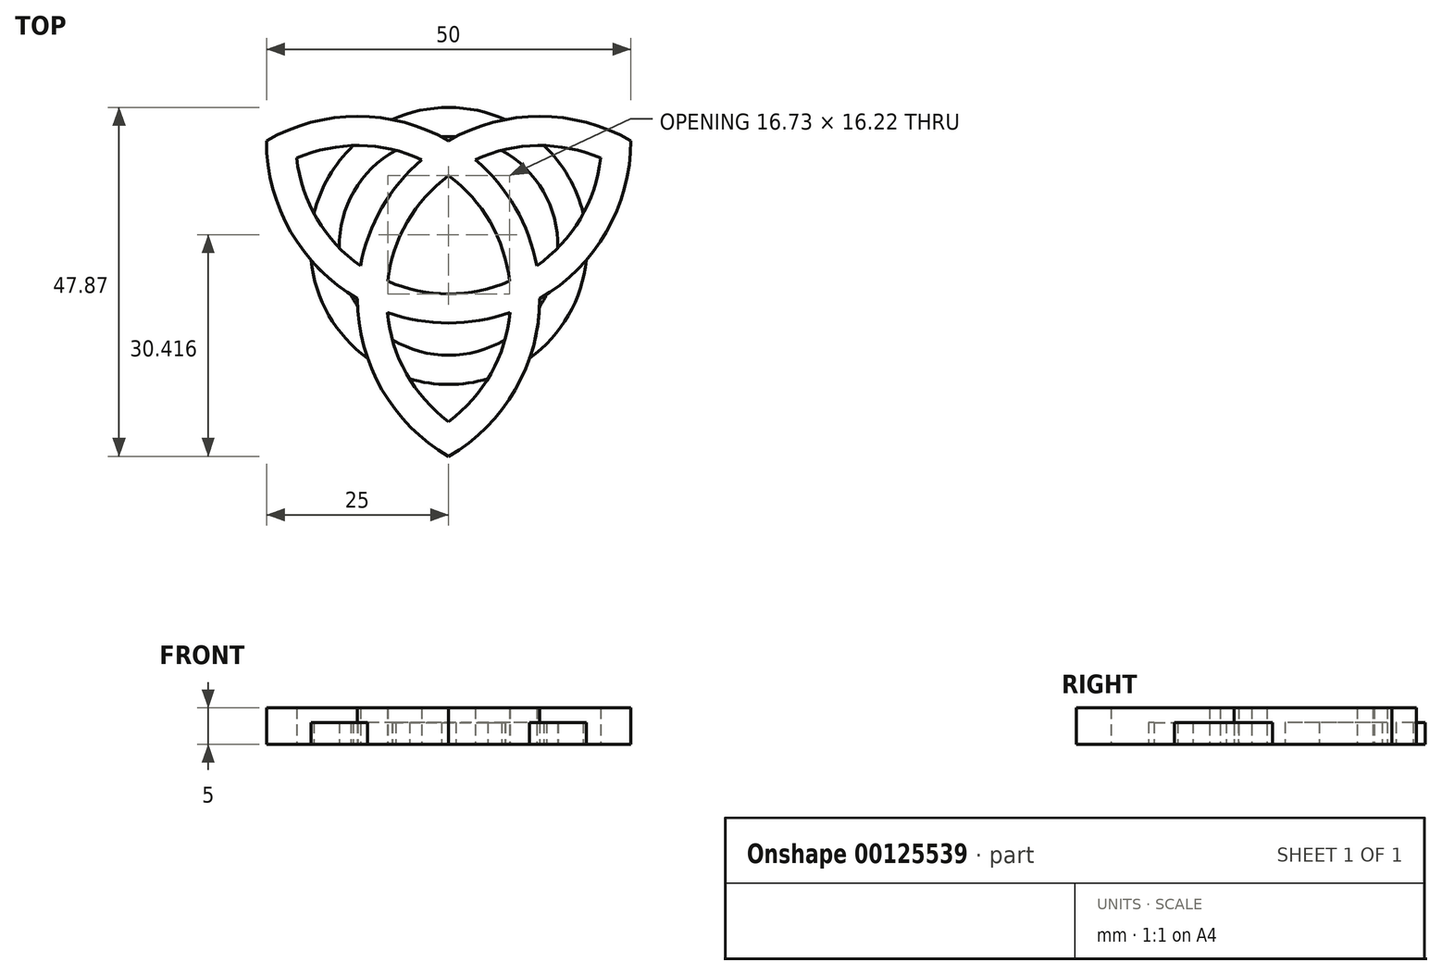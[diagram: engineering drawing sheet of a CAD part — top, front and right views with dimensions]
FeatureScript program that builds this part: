
annotation { "Feature Type Name" : "Feature", "Feature Type Description" : "" }
export const myFeature = defineFeature(function(context is Context, id is Id, definition is map)
    precondition{}
    {
        {
            var Q0;
            Q0=qCreatedBy(makeId("Top.planeOp"),FACE);
            var sketch = newSketch(context, id + "F0", { "sketchPlane" : qUnion([Q0])});
            skCircle(sketch, "E0.cCircle", {"center": v(0, 0) * mm, "radius": 14.43 * mm, "construction": true});
            skLineSegment(sketch, "E0.0", {"start": v(-25, 14.43) * mm, "end": v(25, 14.43) * mm, "construction": true});
            skLineSegment(sketch, "E0.1", {"start": v(25, 14.43) * mm, "end": v(0, -28.87) * mm, "construction": true});
            skLineSegment(sketch, "E0.2", {"start": v(0, -28.87) * mm, "end": v(-25, 14.43) * mm, "construction": true});
            skPoint(sketch, "E0.0.midPoint", {"position": v(0, 14.43) * mm});
            skCircle(sketch, "E1", {"center": v(0, 14.43) * mm, "radius": 25 * mm});
            skCircle(sketch, "E2", {"center": v(12.5, -7.22) * mm, "radius": 25 * mm});
            skCircle(sketch, "E3", {"center": v(-12.5, -7.22) * mm, "radius": 25 * mm});
            skCircle(sketch, "E4.0", {"center": v(-12.5, -7.22) * mm, "radius": 21 * mm});
            skCircle(sketch, "E5.0", {"center": v(0, 14.43) * mm, "radius": 21 * mm});
            skCircle(sketch, "E6.0", {"center": v(12.5, -7.22) * mm, "radius": 21 * mm});
            skCircle(sketch, "E7", {"center": v(0, 0) * mm, "radius": 19 * mm});
            skCircle(sketch, "E8.0", {"center": v(0, 0) * mm, "radius": 15 * mm});
            skSolve(sketch);
        }
        {
            var Q0;
            {var subQ0=sQuery(id+"F0.wireOp",EDGE,"E2");var subQ1=sQuery(id+"F0.wireOp",EDGE,"E1");var subQ2=makeQuery(id+"F0.imprint","INTERSECT",VERTEX,{"disambiguationData":[OD(0.0)],"derivedFrom":[subQ1,subQ0]});Q0=makeQuery(id+"F0.imprint","IMPRINT",FACE,{"disambiguationData":[TD([[makeQuery(id+"F0.imprint","IMPRINT",EDGE,{"disambiguationData":[TD([[subQ2,1.0]])],"derivedFrom":subQ1}),1.0]])]});}
            var Q1;
            {var subQ0=sQuery(id+"F0.wireOp",EDGE,"E7");var subQ1=sQuery(id+"F0.wireOp",EDGE,"E1");var subQ2=makeQuery(id+"F0.imprint","INTERSECT",VERTEX,{"disambiguationData":[OD(1.0)],"derivedFrom":[subQ1,subQ0]});Q1=makeQuery(id+"F0.imprint","IMPRINT",FACE,{"disambiguationData":[TD([[makeQuery(id+"F0.imprint","IMPRINT",EDGE,{"disambiguationData":[TD([[subQ2,-1.0]])],"derivedFrom":subQ1}),1.0]])]});}
            var Q2;
            {var subQ0=sQuery(id+"F0.wireOp",EDGE,"E8.0");var subQ1=sQuery(id+"F0.wireOp",EDGE,"E1");var subQ2=makeQuery(id+"F0.imprint","INTERSECT",VERTEX,{"disambiguationData":[OD(1.0)],"derivedFrom":[subQ1,subQ0]});Q2=makeQuery(id+"F0.imprint","IMPRINT",FACE,{"disambiguationData":[TD([[makeQuery(id+"F0.imprint","IMPRINT",EDGE,{"disambiguationData":[TD([[subQ2,-1.0]])],"derivedFrom":subQ1}),1.0]])]});}
            var Q3;
            {var subQ0=sQuery(id+"F0.wireOp",EDGE,"E3");var subQ1=sQuery(id+"F0.wireOp",EDGE,"E1");var subQ2=makeQuery(id+"F0.imprint","INTERSECT",VERTEX,{"disambiguationData":[OD(1.0)],"derivedFrom":[subQ1,subQ0]});Q3=makeQuery(id+"F0.imprint","IMPRINT",FACE,{"disambiguationData":[TD([[makeQuery(id+"F0.imprint","IMPRINT",EDGE,{"disambiguationData":[TD([[subQ2,-1.0]])],"derivedFrom":subQ1}),1.0]])]});}
            var Q4;
            {var subQ0=sQuery(id+"F0.wireOp",EDGE,"E4.0");var subQ1=sQuery(id+"F0.wireOp",EDGE,"E1");var subQ2=makeQuery(id+"F0.imprint","INTERSECT",VERTEX,{"disambiguationData":[OD(1.0)],"derivedFrom":[subQ1,subQ0]});Q4=makeQuery(id+"F0.imprint","IMPRINT",FACE,{"disambiguationData":[TD([[makeQuery(id+"F0.imprint","IMPRINT",EDGE,{"disambiguationData":[TD([[subQ2,-1.0]])],"derivedFrom":subQ1}),1.0]])]});}
            var Q5;
            {var subQ0=sQuery(id+"F0.wireOp",EDGE,"E6.0");var subQ1=sQuery(id+"F0.wireOp",EDGE,"E1");var subQ2=makeQuery(id+"F0.imprint","INTERSECT",VERTEX,{"disambiguationData":[OD(0.0)],"derivedFrom":[subQ1,subQ0]});Q5=makeQuery(id+"F0.imprint","IMPRINT",FACE,{"disambiguationData":[TD([[makeQuery(id+"F0.imprint","IMPRINT",EDGE,{"disambiguationData":[TD([[subQ2,-1.0]])],"derivedFrom":subQ1}),1.0]])]});}
            var Q6;
            {var subQ0=sQuery(id+"F0.wireOp",EDGE,"E2");var subQ1=sQuery(id+"F0.wireOp",EDGE,"E1");var subQ2=makeQuery(id+"F0.imprint","INTERSECT",VERTEX,{"disambiguationData":[OD(1.0)],"derivedFrom":[subQ1,subQ0]});Q6=makeQuery(id+"F0.imprint","IMPRINT",FACE,{"disambiguationData":[TD([[makeQuery(id+"F0.imprint","IMPRINT",EDGE,{"disambiguationData":[TD([[subQ2,-1.0]])],"derivedFrom":subQ1}),1.0]])]});}
            var Q7;
            {var subQ0=sQuery(id+"F0.wireOp",EDGE,"E8.0");var subQ1=sQuery(id+"F0.wireOp",EDGE,"E1");var subQ2=makeQuery(id+"F0.imprint","INTERSECT",VERTEX,{"disambiguationData":[OD(0.0)],"derivedFrom":[subQ1,subQ0]});Q7=makeQuery(id+"F0.imprint","IMPRINT",FACE,{"disambiguationData":[TD([[makeQuery(id+"F0.imprint","IMPRINT",EDGE,{"disambiguationData":[TD([[subQ2,-1.0]])],"derivedFrom":subQ1}),1.0]])]});}
            var Q8;
            {var subQ0=sQuery(id+"F0.wireOp",EDGE,"E7");var subQ1=sQuery(id+"F0.wireOp",EDGE,"E1");var subQ2=makeQuery(id+"F0.imprint","INTERSECT",VERTEX,{"disambiguationData":[OD(0.0)],"derivedFrom":[subQ1,subQ0]});Q8=makeQuery(id+"F0.imprint","IMPRINT",FACE,{"disambiguationData":[TD([[makeQuery(id+"F0.imprint","IMPRINT",EDGE,{"disambiguationData":[TD([[subQ2,-1.0]])],"derivedFrom":subQ1}),1.0]])]});}
            var Q9;
            {var subQ0=sQuery(id+"F0.wireOp",EDGE,"E4.0");var subQ1=sQuery(id+"F0.wireOp",EDGE,"E1");var subQ2=makeQuery(id+"F0.imprint","INTERSECT",VERTEX,{"disambiguationData":[OD(0.0)],"derivedFrom":[subQ1,subQ0]});Q9=makeQuery(id+"F0.imprint","IMPRINT",FACE,{"disambiguationData":[TD([[makeQuery(id+"F0.imprint","IMPRINT",EDGE,{"disambiguationData":[TD([[subQ2,-1.0]])],"derivedFrom":subQ1}),1.0]])]});}
            var Q10;
            {var subQ0=sQuery(id+"F0.wireOp",EDGE,"E3");var subQ1=sQuery(id+"F0.wireOp",EDGE,"E1");var subQ2=makeQuery(id+"F0.imprint","INTERSECT",VERTEX,{"disambiguationData":[OD(0.0)],"derivedFrom":[subQ1,subQ0]});Q10=makeQuery(id+"F0.imprint","IMPRINT",FACE,{"disambiguationData":[TD([[makeQuery(id+"F0.imprint","IMPRINT",EDGE,{"disambiguationData":[TD([[subQ2,-1.0]])],"derivedFrom":subQ1}),1.0]])]});}
            var Q11;
            {var subQ0=sQuery(id+"F0.wireOp",EDGE,"E7");var subQ1=sQuery(id+"F0.wireOp",EDGE,"E3");var subQ2=makeQuery(id+"F0.imprint","INTERSECT",VERTEX,{"disambiguationData":[OD(0.0)],"derivedFrom":[subQ1,subQ0]});Q11=makeQuery(id+"F0.imprint","IMPRINT",FACE,{"disambiguationData":[TD([[makeQuery(id+"F0.imprint","IMPRINT",EDGE,{"disambiguationData":[TD([[subQ2,-1.0]])],"derivedFrom":subQ1}),1.0]])]});}
            var Q12;
            {var subQ0=sQuery(id+"F0.wireOp",EDGE,"E8.0");var subQ1=sQuery(id+"F0.wireOp",EDGE,"E3");var subQ2=makeQuery(id+"F0.imprint","INTERSECT",VERTEX,{"disambiguationData":[OD(0.0)],"derivedFrom":[subQ1,subQ0]});Q12=makeQuery(id+"F0.imprint","IMPRINT",FACE,{"disambiguationData":[TD([[makeQuery(id+"F0.imprint","IMPRINT",EDGE,{"disambiguationData":[TD([[subQ2,-1.0]])],"derivedFrom":subQ1}),1.0]])]});}
            var Q13;
            {var subQ0=sQuery(id+"F0.wireOp",EDGE,"E3");var subQ1=sQuery(id+"F0.wireOp",EDGE,"E2");var subQ2=makeQuery(id+"F0.imprint","INTERSECT",VERTEX,{"disambiguationData":[OD(1.0)],"derivedFrom":[subQ1,subQ0]});Q13=makeQuery(id+"F0.imprint","IMPRINT",FACE,{"disambiguationData":[TD([[makeQuery(id+"F0.imprint","IMPRINT",EDGE,{"disambiguationData":[TD([[subQ2,-1.0]])],"derivedFrom":subQ1}),-1.0]])]});}
            var Q14;
            {var subQ0=sQuery(id+"F0.wireOp",EDGE,"E3");var subQ1=sQuery(id+"F0.wireOp",EDGE,"E2");var subQ2=makeQuery(id+"F0.imprint","INTERSECT",VERTEX,{"disambiguationData":[OD(1.0)],"derivedFrom":[subQ1,subQ0]});Q14=makeQuery(id+"F0.imprint","IMPRINT",FACE,{"disambiguationData":[TD([[makeQuery(id+"F0.imprint","IMPRINT",EDGE,{"disambiguationData":[TD([[subQ2,-1.0]])],"derivedFrom":subQ1}),1.0]])]});}
            var Q15;
            {var subQ0=sQuery(id+"F0.wireOp",EDGE,"E5.0");var subQ1=sQuery(id+"F0.wireOp",EDGE,"E3");var subQ2=makeQuery(id+"F0.imprint","INTERSECT",VERTEX,{"disambiguationData":[OD(0.0)],"derivedFrom":[subQ1,subQ0]});Q15=makeQuery(id+"F0.imprint","IMPRINT",FACE,{"disambiguationData":[TD([[makeQuery(id+"F0.imprint","IMPRINT",EDGE,{"disambiguationData":[TD([[subQ2,-1.0]])],"derivedFrom":subQ1}),1.0]])]});}
            var Q16;
            {var subQ0=sQuery(id+"F0.wireOp",EDGE,"E4.0");var subQ1=sQuery(id+"F0.wireOp",EDGE,"E1");var subQ2=makeQuery(id+"F0.imprint","INTERSECT",VERTEX,{"disambiguationData":[OD(1.0)],"derivedFrom":[subQ1,subQ0]});Q16=makeQuery(id+"F0.imprint","IMPRINT",FACE,{"disambiguationData":[TD([[makeQuery(id+"F0.imprint","IMPRINT",EDGE,{"disambiguationData":[TD([[subQ2,-1.0]])],"derivedFrom":subQ1}),-1.0]])]});}
            var Q17;
            {var subQ0=sQuery(id+"F0.wireOp",EDGE,"E7");var subQ1=sQuery(id+"F0.wireOp",EDGE,"E3");var subQ2=makeQuery(id+"F0.imprint","INTERSECT",VERTEX,{"disambiguationData":[OD(1.0)],"derivedFrom":[subQ1,subQ0]});Q17=makeQuery(id+"F0.imprint","IMPRINT",FACE,{"disambiguationData":[TD([[makeQuery(id+"F0.imprint","IMPRINT",EDGE,{"disambiguationData":[TD([[subQ2,-1.0]])],"derivedFrom":subQ1}),1.0]])]});}
            var Q18;
            {var subQ0=sQuery(id+"F0.wireOp",EDGE,"E6.0");var subQ1=sQuery(id+"F0.wireOp",EDGE,"E3");var subQ2=makeQuery(id+"F0.imprint","INTERSECT",VERTEX,{"disambiguationData":[OD(1.0)],"derivedFrom":[subQ1,subQ0]});Q18=makeQuery(id+"F0.imprint","IMPRINT",FACE,{"disambiguationData":[TD([[makeQuery(id+"F0.imprint","IMPRINT",EDGE,{"disambiguationData":[TD([[subQ2,-1.0]])],"derivedFrom":subQ1}),1.0]])]});}
            var Q19;
            {var subQ0=sQuery(id+"F0.wireOp",EDGE,"E3");var subQ1=sQuery(id+"F0.wireOp",EDGE,"E2");var subQ2=makeQuery(id+"F0.imprint","INTERSECT",VERTEX,{"disambiguationData":[OD(0.0)],"derivedFrom":[subQ1,subQ0]});Q19=makeQuery(id+"F0.imprint","IMPRINT",FACE,{"disambiguationData":[TD([[makeQuery(id+"F0.imprint","IMPRINT",EDGE,{"disambiguationData":[TD([[subQ2,1.0]])],"derivedFrom":subQ1}),1.0]])]});}
            var Q20;
            {var subQ0=sQuery(id+"F0.wireOp",EDGE,"E7");var subQ1=sQuery(id+"F0.wireOp",EDGE,"E2");var subQ2=makeQuery(id+"F0.imprint","INTERSECT",VERTEX,{"disambiguationData":[OD(1.0)],"derivedFrom":[subQ1,subQ0]});Q20=makeQuery(id+"F0.imprint","IMPRINT",FACE,{"disambiguationData":[TD([[makeQuery(id+"F0.imprint","IMPRINT",EDGE,{"disambiguationData":[TD([[subQ2,-1.0]])],"derivedFrom":subQ1}),1.0]])]});}
            var Q21;
            {var subQ0=sQuery(id+"F0.wireOp",EDGE,"E8.0");var subQ1=sQuery(id+"F0.wireOp",EDGE,"E2");var subQ2=makeQuery(id+"F0.imprint","INTERSECT",VERTEX,{"disambiguationData":[OD(1.0)],"derivedFrom":[subQ1,subQ0]});Q21=makeQuery(id+"F0.imprint","IMPRINT",FACE,{"disambiguationData":[TD([[makeQuery(id+"F0.imprint","IMPRINT",EDGE,{"disambiguationData":[TD([[subQ2,-1.0]])],"derivedFrom":subQ1}),1.0]])]});}
            var Q22;
            {var subQ0=sQuery(id+"F0.wireOp",EDGE,"E2");var subQ1=sQuery(id+"F0.wireOp",EDGE,"E1");var subQ2=makeQuery(id+"F0.imprint","INTERSECT",VERTEX,{"disambiguationData":[OD(1.0)],"derivedFrom":[subQ1,subQ0]});Q22=makeQuery(id+"F0.imprint","IMPRINT",FACE,{"disambiguationData":[TD([[makeQuery(id+"F0.imprint","IMPRINT",EDGE,{"disambiguationData":[TD([[subQ2,-1.0]])],"derivedFrom":subQ1}),-1.0]])]});}
            var Q23;
            {var subQ0=sQuery(id+"F0.wireOp",EDGE,"E4.0");var subQ1=sQuery(id+"F0.wireOp",EDGE,"E2");var subQ2=makeQuery(id+"F0.imprint","INTERSECT",VERTEX,{"disambiguationData":[OD(0.0)],"derivedFrom":[subQ1,subQ0]});Q23=makeQuery(id+"F0.imprint","IMPRINT",FACE,{"disambiguationData":[TD([[makeQuery(id+"F0.imprint","IMPRINT",EDGE,{"disambiguationData":[TD([[subQ2,-1.0]])],"derivedFrom":subQ1}),1.0]])]});}
            var Q24;
            {var subQ0=sQuery(id+"F0.wireOp",EDGE,"E8.0");var subQ1=sQuery(id+"F0.wireOp",EDGE,"E2");var subQ2=makeQuery(id+"F0.imprint","INTERSECT",VERTEX,{"disambiguationData":[OD(0.0)],"derivedFrom":[subQ1,subQ0]});Q24=makeQuery(id+"F0.imprint","IMPRINT",FACE,{"disambiguationData":[TD([[makeQuery(id+"F0.imprint","IMPRINT",EDGE,{"disambiguationData":[TD([[subQ2,-1.0]])],"derivedFrom":subQ1}),1.0]])]});}
            var Q25;
            {var subQ0=sQuery(id+"F0.wireOp",EDGE,"E7");var subQ1=sQuery(id+"F0.wireOp",EDGE,"E2");var subQ2=makeQuery(id+"F0.imprint","INTERSECT",VERTEX,{"disambiguationData":[OD(0.0)],"derivedFrom":[subQ1,subQ0]});Q25=makeQuery(id+"F0.imprint","IMPRINT",FACE,{"disambiguationData":[TD([[makeQuery(id+"F0.imprint","IMPRINT",EDGE,{"disambiguationData":[TD([[subQ2,-1.0]])],"derivedFrom":subQ1}),1.0]])]});}
            var Q26;
            {var subQ0=sQuery(id+"F0.wireOp",EDGE,"E5.0");var subQ1=sQuery(id+"F0.wireOp",EDGE,"E2");var subQ2=makeQuery(id+"F0.imprint","INTERSECT",VERTEX,{"disambiguationData":[OD(0.0)],"derivedFrom":[subQ1,subQ0]});Q26=makeQuery(id+"F0.imprint","IMPRINT",FACE,{"disambiguationData":[TD([[makeQuery(id+"F0.imprint","IMPRINT",EDGE,{"disambiguationData":[TD([[subQ2,-1.0]])],"derivedFrom":subQ1}),1.0]])]});}
            extrude(context, id + "F1", {"entities" : qUnion([Q0, Q1, Q2, Q3, Q4, Q5, Q6, Q7, Q8, Q9, Q10, Q11, Q12, Q13, Q14, Q15, Q16, Q17, Q18, Q19, Q20, Q21, Q22, Q23, Q24, Q25, Q26]), "depth" : 5 * mm});
        }
        {
            var Q0;
            {var subQ0=sQuery(id+"F0.wireOp",EDGE,"E7");var subQ1=sQuery(id+"F0.wireOp",EDGE,"E2");var subQ2=makeQuery(id+"F0.imprint","INTERSECT",VERTEX,{"disambiguationData":[OD(0.0)],"derivedFrom":[subQ1,subQ0]});Q0=makeQuery(id+"F0.imprint","IMPRINT",FACE,{"disambiguationData":[TD([[makeQuery(id+"F0.imprint","IMPRINT",EDGE,{"disambiguationData":[TD([[subQ2,-1.0]])],"derivedFrom":subQ1}),-1.0]])]});}
            var Q1;
            {var subQ0=sQuery(id+"F0.wireOp",EDGE,"E8.0");var subQ1=sQuery(id+"F0.wireOp",EDGE,"E5.0");var subQ2=makeQuery(id+"F0.imprint","INTERSECT",VERTEX,{"disambiguationData":[OD(1.0)],"derivedFrom":[subQ1,subQ0]});Q1=makeQuery(id+"F0.imprint","IMPRINT",FACE,{"disambiguationData":[TD([[makeQuery(id+"F0.imprint","IMPRINT",EDGE,{"disambiguationData":[TD([[subQ2,-1.0]])],"derivedFrom":subQ1}),1.0]])]});}
            var Q2;
            {var subQ0=sQuery(id+"F0.wireOp",EDGE,"E8.0");var subQ1=sQuery(id+"F0.wireOp",EDGE,"E1");var subQ2=makeQuery(id+"F0.imprint","INTERSECT",VERTEX,{"disambiguationData":[OD(1.0)],"derivedFrom":[subQ1,subQ0]});Q2=makeQuery(id+"F0.imprint","IMPRINT",FACE,{"disambiguationData":[TD([[makeQuery(id+"F0.imprint","IMPRINT",EDGE,{"disambiguationData":[TD([[subQ2,-1.0]])],"derivedFrom":subQ1}),-1.0]])]});}
            var Q3;
            {var subQ0=sQuery(id+"F0.wireOp",EDGE,"E7");var subQ1=sQuery(id+"F0.wireOp",EDGE,"E4.0");var subQ2=makeQuery(id+"F0.imprint","INTERSECT",VERTEX,{"disambiguationData":[OD(1.0)],"derivedFrom":[subQ1,subQ0]});Q3=makeQuery(id+"F0.imprint","IMPRINT",FACE,{"disambiguationData":[TD([[makeQuery(id+"F0.imprint","IMPRINT",EDGE,{"disambiguationData":[TD([[subQ2,-1.0]])],"derivedFrom":subQ1}),1.0]])]});}
            var Q4;
            {var subQ0=sQuery(id+"F0.wireOp",EDGE,"E7");var subQ1=sQuery(id+"F0.wireOp",EDGE,"E1");var subQ2=makeQuery(id+"F0.imprint","INTERSECT",VERTEX,{"disambiguationData":[OD(0.0)],"derivedFrom":[subQ1,subQ0]});Q4=makeQuery(id+"F0.imprint","IMPRINT",FACE,{"disambiguationData":[TD([[makeQuery(id+"F0.imprint","IMPRINT",EDGE,{"disambiguationData":[TD([[subQ2,-1.0]])],"derivedFrom":subQ1}),-1.0]])]});}
            var Q5;
            {var subQ0=sQuery(id+"F0.wireOp",EDGE,"E8.0");var subQ1=sQuery(id+"F0.wireOp",EDGE,"E4.0");var subQ2=makeQuery(id+"F0.imprint","INTERSECT",VERTEX,{"disambiguationData":[OD(0.0)],"derivedFrom":[subQ1,subQ0]});Q5=makeQuery(id+"F0.imprint","IMPRINT",FACE,{"disambiguationData":[TD([[makeQuery(id+"F0.imprint","IMPRINT",EDGE,{"disambiguationData":[TD([[subQ2,-1.0]])],"derivedFrom":subQ1}),1.0]])]});}
            extrude(context, id + "F2", {"entities" : qUnion([Q0, Q1, Q2, Q3, Q4, Q5]), "operationType" : NewBodyOperationType.ADD, "depth" : 3 * mm});
        }
    });
